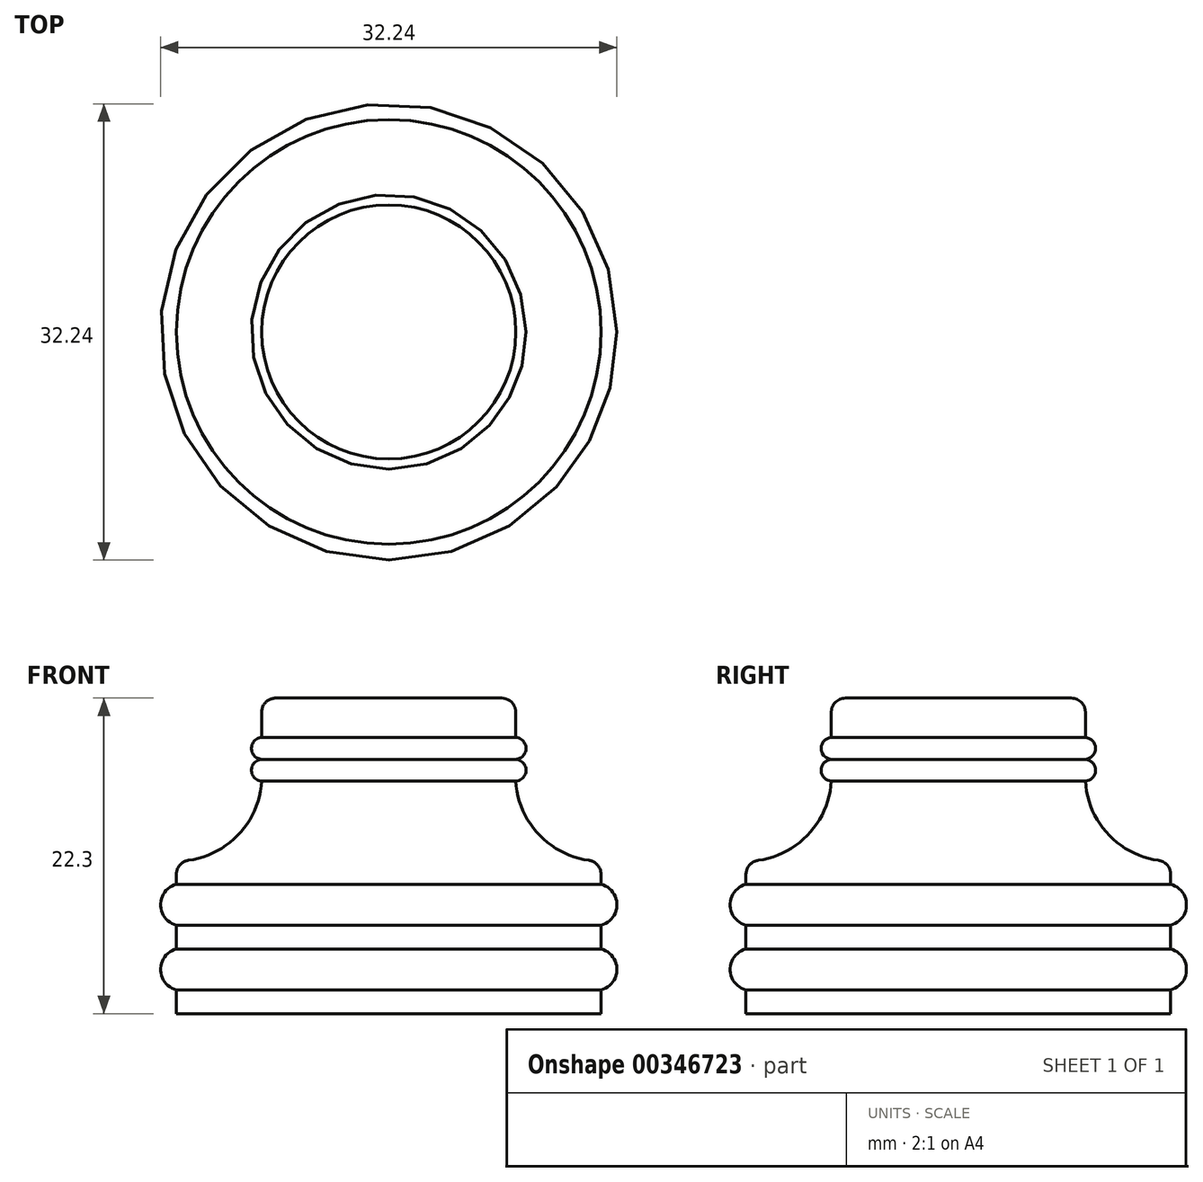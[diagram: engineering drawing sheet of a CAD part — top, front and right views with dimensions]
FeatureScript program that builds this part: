
annotation { "Feature Type Name" : "Feature", "Feature Type Description" : "" }
export const myFeature = defineFeature(function(context is Context, id is Id, definition is map)
    precondition{}
    {
        {
            var Q0;
            Q0=qCreatedBy(makeId("Front.planeOp"),FACE);
            var sketch = newSketch(context, id + "F0", { "sketchPlane" : qUnion([Q0])});
            skLineSegment(sketch, "E0", {"start": v(-63.84, 43.99) * mm, "end": v(-63.84, 21.69) * mm});
            skLineSegment(sketch, "E1", {"start": v(-63.84, 21.69) * mm, "end": v(-48.84, 21.69) * mm});
            skLineSegment(sketch, "E2", {"start": v(-48.84, 21.69) * mm, "end": v(-48.84, 23.36) * mm});
            skArc(sketch, "E3", {"start": v(-48.84, 23.36) * mm, "mid": v(-47.72, 24.8) * mm, "end": v(-48.84, 26.26) * mm});
            skLineSegment(sketch, "E4", {"start": v(-48.84, 26.26) * mm, "end": v(-48.84, 27.93) * mm});
            skArc(sketch, "E5", {"start": v(-48.84, 27.93) * mm, "mid": v(-47.72, 29.38) * mm, "end": v(-48.84, 30.83) * mm});
            skLineSegment(sketch, "E6", {"start": v(-48.84, 30.83) * mm, "end": v(-48.84, 32.53) * mm});
            skLineSegment(sketch, "E7", {"start": v(-48.84, 32.53) * mm, "end": v(-54.86, 32.53) * mm});
            skLineSegment(sketch, "E8", {"start": v(-54.86, 32.53) * mm, "end": v(-54.86, 38.12) * mm});
            skArc(sketch, "E9", {"start": v(-54.86, 38.12) * mm, "mid": v(-54.14, 38.9) * mm, "end": v(-54.86, 39.66) * mm});
            skArc(sketch, "E10", {"start": v(-54.86, 39.66) * mm, "mid": v(-54.14, 40.43) * mm, "end": v(-54.86, 41.2) * mm});
            skLineSegment(sketch, "E11", {"start": v(-54.86, 41.2) * mm, "end": v(-54.86, 43.99) * mm});
            skLineSegment(sketch, "E12", {"start": v(-54.86, 43.99) * mm, "end": v(-63.84, 43.99) * mm});
            skSolve(sketch);
        }
        {
            var Q0;
            Q0=makeQuery(id+"F0.imprint","IMPRINT",FACE,{"disambiguationData":[TD([[makeQuery(id+"F0.imprint","IMPRINT",EDGE,{"derivedFrom":sQuery(id+"F0.wireOp",EDGE,"E0")}),1.0]])]});
            var Q1;
            Q1=sQuery(id+"F0.wireOp",EDGE,"E0");
            revolve(context, id + "F1", {"entities" : qUnion([Q0]), "axis" : qUnion([Q1]), "revolveType" : RevolveType.FULL});
        }
        {
            var Q0;
            Q0=makeQuery(id+"F1.opRevolve","SWEPT_EDGE",EDGE,{"disambiguationData":[OSD([sQuery(id+"F0.wireOp",EDGE,"E6"),sQuery(id+"F0.wireOp",EDGE,"E7")])]});
            fillet(context, id + "F2", {"entities" : qUnion([Q0]), "radius" : 1 * mm, "tangentPropagation" : true, "allowEdgeOverflow" : false});
        }
        {
            var Q0;
            Q0=makeQuery(id+"F1.opRevolve","SWEPT_EDGE",EDGE,{"disambiguationData":[OSD([sQuery(id+"F0.wireOp",EDGE,"E7"),sQuery(id+"F0.wireOp",EDGE,"E8")])]});
            fillet(context, id + "F3", {"entities" : qUnion([Q0]), "radius" : 6 * mm, "tangentPropagation" : true, "allowEdgeOverflow" : false});
        }
        {
            var Q0;
            Q0=makeQuery(id+"F1.opRevolve","SWEPT_EDGE",EDGE,{"disambiguationData":[OSD([sQuery(id+"F0.wireOp",EDGE,"E11"),sQuery(id+"F0.wireOp",EDGE,"E12")])]});
            fillet(context, id + "F4", {"entities" : qUnion([Q0]), "radius" : 1 * mm, "tangentPropagation" : true, "allowEdgeOverflow" : false});
        }
    });
